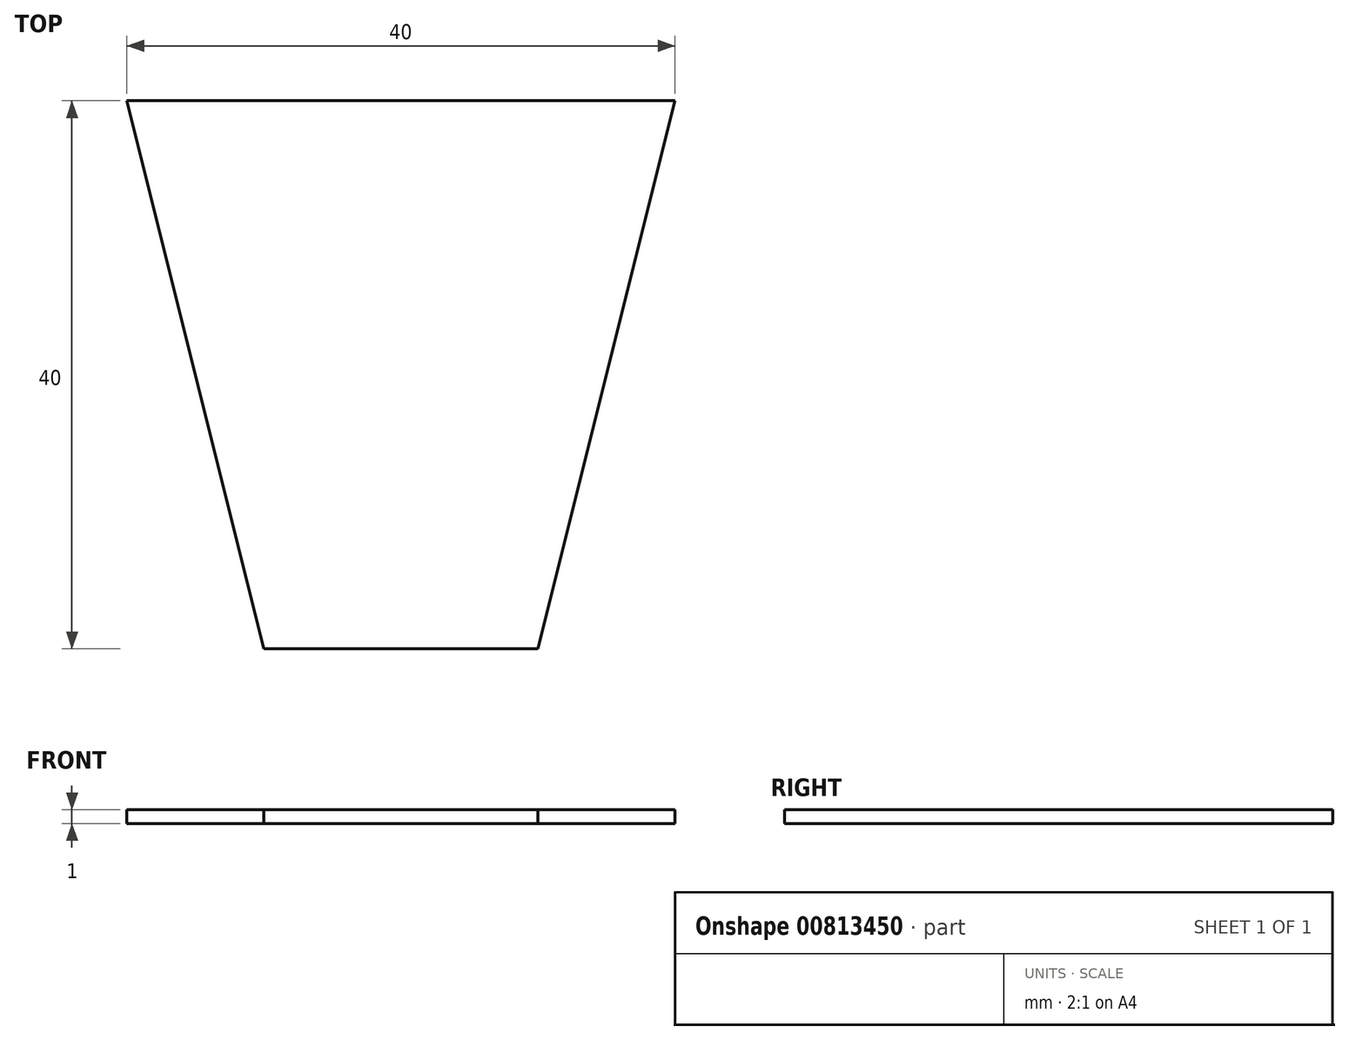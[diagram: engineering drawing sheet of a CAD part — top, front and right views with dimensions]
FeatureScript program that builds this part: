
annotation { "Feature Type Name" : "Feature", "Feature Type Description" : "" }
export const myFeature = defineFeature(function(context is Context, id is Id, definition is map)
    precondition{}
    {
        {
            var Q0;
            Q0=qCreatedBy(makeId("Top.planeOp"),FACE);
            var sketch = newSketch(context, id + "F0", { "sketchPlane" : qUnion([Q0])});
            skLineSegment(sketch, "E0.bottom", {"start": v(20, 20) * mm, "end": v(-20, 20) * mm});
            skLineSegment(sketch, "E0.top", {"start": v(10, -20) * mm, "end": v(-10, -20) * mm});
            skPoint(sketch, "E0.middle", {"position": v(0, 0) * mm});
            skLineSegment(sketch, "E1", {"start": v(-20, 20) * mm, "end": v(-10, -20) * mm});
            skLineSegment(sketch, "E2", {"start": v(10, -20) * mm, "end": v(20, 20) * mm});
            skPoint(sketch, "E3.orphan", {"position": v(-20, -20) * mm});
            skPoint(sketch, "E4.orphan", {"position": v(20, -20) * mm});
            skSolve(sketch);
        }
        {
            var Q0;
            Q0=makeQuery(id+"F0.imprint","IMPRINT",FACE,{"disambiguationData":[TD([[makeQuery(id+"F0.imprint","IMPRINT",EDGE,{"derivedFrom":sQuery(id+"F0.wireOp",EDGE,"E0.bottom")}),1.0]])]});
            extrude(context, id + "F1", {"entities" : qUnion([Q0]), "depth" : 1 * mm, "offsetDistance" : 25 * mm});
        }
    });
